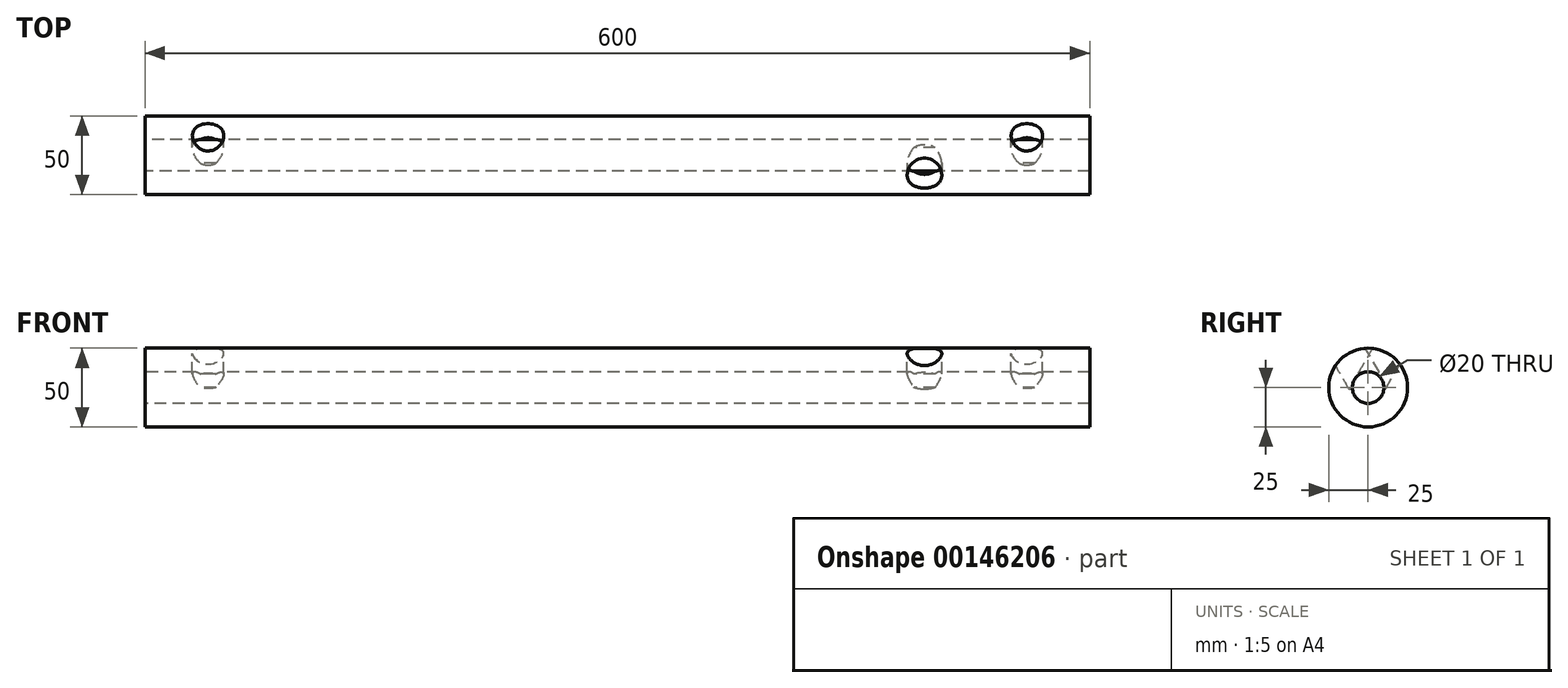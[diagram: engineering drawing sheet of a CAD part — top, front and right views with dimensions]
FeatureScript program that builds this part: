
annotation { "Feature Type Name" : "Feature", "Feature Type Description" : "" }
export const myFeature = defineFeature(function(context is Context, id is Id, definition is map)
    precondition{}
    {
        {
            var Q0;
            Q0=qCreatedBy(makeId("Right.planeOp"),FACE);
            var sketch = newSketch(context, id + "F0", { "sketchPlane" : qUnion([Q0])});
            skCircle(sketch, "E0", {"center": v(0, 0) * mm, "radius": 25 * mm});
            skCircle(sketch, "E1", {"center": v(0, 0) * mm, "radius": 10 * mm});
            skLineSegment(sketch, "E2", {"start": v(0, 0) * mm, "end": v(-12.5, 21.65) * mm});
            skLineSegment(sketch, "E3.MirrorCS", {"start": v(0, 0) * mm, "end": v(12.5, 21.65) * mm});
            skLineSegment(sketch, "E4", {"start": v(-8.17, 24.15) * mm, "end": v(-16.83, 19.15) * mm});
            skLineSegment(sketch, "E5.MirrorCS", {"start": v(8.17, 24.15) * mm, "end": v(16.83, 19.15) * mm});
            skSolve(sketch);
        }
        {
            var Q0;
            Q0=makeQuery(id+"F0.imprint","IMPRINT",FACE,{"disambiguationData":[TD([[makeQuery(id+"F0.imprint","IMPRINT",EDGE,{"derivedFrom":sQuery(id+"F0.wireOp",EDGE,"E0")}),1.0]])]});
            extrude(context, id + "F1", {"entities" : qUnion([Q0]), "depth" : 600 * mm, "symmetric" : true});
        }
        {
            var Q0;
            Q0=sQuery(id+"F0.wireOp",EDGE,"E4");
            var Q1;
            Q1=makeQuery(id+"F1.opExtrude","SWEPT_FACE",FACE,{"disambiguationData":[OSD([sQuery(id+"F0.wireOp",EDGE,"E0")])]});
            cPlane(context, id + "F2", {"entities" : qUnion([Q0, Q1]), "cplaneType" : CPlaneType.LINE_ANGLE, "offset" : 25.4 * mm, "angle" : 0 * degree, "width" : 152.4 * mm, "height" : 152.4 * mm});
        }
        {
            var Q0;
            Q0=qCreatedBy(id+"F2.planeOp",FACE);
            var sketch = newSketch(context, id + "F3", { "sketchPlane" : qUnion([Q0])});
            skLineSegment(sketch, "E6", {"start": v(195, 0) * mm, "end": v(-195, 0) * mm});
            skCircle(sketch, "E7", {"center": v(195, 0) * mm, "radius": 11 * mm});
            skCircle(sketch, "E8.MirrorC", {"center": v(-195, 0) * mm, "radius": 11 * mm});
            skSolve(sketch);
        }
        {
            var Q0;
            Q0=makeQuery(id+"F3.imprint","IMPRINT",FACE,{"disambiguationData":[TD([[makeQuery(id+"F3.imprint","IMPRINT",EDGE,{"derivedFrom":sQuery(id+"F3.wireOp",EDGE,"E7")}),1.0]])]});
            var Q1;
            Q1=makeQuery(id+"F3.imprint","IMPRINT",FACE,{"disambiguationData":[TD([[makeQuery(id+"F3.imprint","IMPRINT",EDGE,{"derivedFrom":sQuery(id+"F3.wireOp",EDGE,"E8.MirrorC")}),-1.0]])]});
            var Q2;
            Q2=sQuery(id+"F3.wireOp",EDGE,"E7");
            var Q3;
            Q3=sQuery(id+"F3.wireOp",EDGE,"E8.MirrorC");
            extrude(context, id + "F4", {"entities" : qUnion([Q0, Q1]), "operationType" : NewBodyOperationType.REMOVE, "surfaceEntities" : qUnion([Q2, Q3]), "depth" : 20 * mm});
        }
        {
            var Q0;
            Q0=sQuery(id+"F0.wireOp",EDGE,"E5.MirrorCS");
            var Q1;
            Q1=makeQuery(id+"F1.opExtrude","SWEPT_FACE",FACE,{"disambiguationData":[OSD([sQuery(id+"F0.wireOp",EDGE,"E0")])]});
            cPlane(context, id + "F5", {"entities" : qUnion([Q0, Q1]), "cplaneType" : CPlaneType.LINE_ANGLE, "offset" : 25.4 * mm, "angle" : 0 * degree, "width" : 152.4 * mm, "height" : 152.4 * mm});
        }
        {
            var Q0;
            Q0=qCreatedBy(id+"F5.planeOp",FACE);
            var sketch = newSketch(context, id + "F6", { "sketchPlane" : qUnion([Q0])});
            skLineSegment(sketch, "E9", {"start": v(-260, 0) * mm, "end": v(260, 0) * mm});
            skCircle(sketch, "E10", {"center": v(-260, 0) * mm, "radius": 10 * mm});
            skCircle(sketch, "E11.MirrorC", {"center": v(260, 0) * mm, "radius": 10 * mm});
            skSolve(sketch);
        }
        {
            var Q0;
            Q0 = qSketchRegion(id + "F6", true);
            extrude(context, id + "F7", {"entities" : qUnion([Q0]), "operationType" : NewBodyOperationType.REMOVE, "oppositeDirection" : true, "depth" : 20 * mm});
        }
    });
